# Revit family: Hager-Vega_D-IP55-syst-FR-fr
name_source: partatom
category: Electrical Equipment
units: mm (PartAtom-declared; Revit-internal decimal feet)

## family parameters
Cut with Voids When Loaded = No
Host = Face
Panel Configuration = Two Columns, Circuits Across
Part Type = Panelboard
Room Calculation Point = No
Round Connector Dimension = Use Diameter
Shared = No

## types (5) — shared parameters
EF000003 - mode de pose = EV000384 - saillie
EF000007 - couleur = EV000202 - blanc
EF000008 - largeur = 550 mm
EF000049 - profondeur = 275 mm  [stored 0.902231 ft]
EF000116 - numéro RAL = 9010
EF000118 - avec cadre/support de montage = No
EF000339 - type de capot = EV004216 - porte
EF001062 - finition CEM = No
EF001088 - possibilité de montage en saillie = Yes
EF001131 - profondeur intérieure = 218 mm
EF001134 - rail DIN = Yes
EF001596 - matériau du boîtier/corps = EV000154 - autre
EF002950 - largeur en nombre de modules = 24
EF004462 - type de fermeture = EV000154 - autre
EF005474 - indice de protection (IP) = EV006420 - IP55
EF006244 - couvercle/porte transparent(e) = No
EF006306 - avec serrure = No
EF009212 - finition du couvercle = EV000116 - fermé
EF015776 - borne de mise à la terre = Yes
EF015777 - borne à conducteur neutre = No
EF015941 - porte pour transmission du signal = No
HG000001 - nombre de colonnes = 1
HG000002 - avec porte = Yes
HG000003 - Gamme = Vega D
HG000005 - Epaisseur = 3 mm  [stored 0.00984252 ft]
HG000006 - Encastré = No
HG000008 - Nombre de rangées vides = 2
HG000009 - Porte à double battant = No
HG000010 - Portes asymétriques = No
HG000011 - Rangées du bas vides = No
HG000017 - Distance entre pôles = 18 mm  [stored 0.0590551 ft]
Manufacturer = Hager
Type Comments = Vega D
zero-valued in all types: Default Elevation, EF000218 - profondeur d'encastrement, EF000332 - hauteur d'encastrement, EF000846 - largeur d'encastrement, HG000007 - Nombre de colonnes vides

## per-type parameters (varying)
| type | EF000040 - hauteur | EF000266 - nombre de rangées | HG000004 - Référence fabricant | Model |
| Saillie IP55 L550 H1100 P275 24 Modules - FV62A | 1100 mm | 4 | FV62A | FV62A |
| Saillie IP55 L550 H1250 P275 24 Modules - FV72A | 1250 mm  [stored 4.10105 ft] | 5 | FV72A | FV72A |
| Saillie IP55 L550 H650 P275 24 Modules - FV32A | 650 mm | 1 | FV32A | FV32A |
| Saillie IP55 L550 H800 P275 24 Modules - FV42A | 800 mm | 2 | FV42A | FV42A |
| Saillie IP55 L550 H950 P275 24 Modules - FV52A | 950 mm  [stored 3.1168 ft] | 3 | FV52A | FV52A |

note: [stored X ft] marks values corroborated as IEEE doubles in the binary element streams (Revit-internal decimal feet)

## geometry (parser evidence)
native form markers: Sweep x17
no freeform markers — native parametric forms only
